# Revit family: ewf_ewg-40_60eta2_fta2-h_60Hz
name_source: partatom
category: 機械設備
units: mm (PartAtom-declared; Revit-internal decimal feet)

## family parameters
OmniClass タイトル = Industrial Ventilating Equipment
OmniClass 番号 = 23.75.35.21.17
パーツ タイプ = 標準
ロード時にボイドで切り取り = はい
丸型コネクタ寸法 = 直径を使用
作業面ベース = いいえ
共有 = いいえ
常に垂直 = はい
部屋計算ポイント = はい

## types (6) — shared parameters
IfcExportAs = IfcFanType
IfcExportType = TUBEAXIAL
MID風量 = 0.0 m³/h
MIN風量 = 0.0 m³/h
OmniClassCode = 23-33 31 19 11 17
URL = https://www.mitsubishielectric.co.jp
Uniclass2015Code = Pr_65_67_29_67
Uniclass2015Title = Propeller fans
Uniclass2015Version = Systems v1.9
ファンの種類 = 軸流羽根
フレームの厚さ = 10  [stored 0.0328084 ft]
仕様書バージョン = Version1.0
企業コード = 108420
分類コード = 50052503100110
周波数 = 60 Hz
呼称 = 有圧扇
極数 = 3
法定耐用年数 = 15
相 = 3
製品リリース年月 = 2022年6月1日
製品出荷対象 = 国内
製造元 = 三菱電機株式会社
設置方法 = 壁付
説明 = 産業用有圧換気扇 低騒音形 耐熱タイプ 排気専用
負荷分類 = 3_ファン類
運転質量 = 0.00 kg

## per-type parameters (varying)
| type | Depth | Height | MAX風量 | Width | オリフィス_Depth | オリフィス径 | モデル | モーター径 | レグ_Depth | レグ_Height | レグ_Width | 価格 | 極 | 消費電力 | 羽根径 | 製品質量 | 質量 | 電動機出力 | 電圧 |
| EWF-40ETA2-H_200V | 308  [stored 1.0105 ft] | 520  [stored 1.70604 ft] | 5520.0 m³/h | 520  [stored 1.70604 ft] | 99  [stored 0.324803 ft] | 480  [stored 1.5748 ft] | EWF-40ETA2-H | 131  [stored 0.42979 ft] | 279 | 416  [stored 1.36483 ft] | 416  [stored 1.36483 ft] | 185000 $ | 4 | 325 W | ∅400 | 16.60 kg | 19.92 kg | 400 W | 200 V |
| EWF-50FTA2-H_200V | 327 | 620  [stored 2.03412 ft] | 8280.0 m³/h | 620  [stored 2.03412 ft] | 84  [stored 0.275591 ft] | 590  [stored 1.9357 ft] | EWF-50FTA2-H | 200  [stored 0.656168 ft] | 242  [stored 0.793963 ft] | 516  [stored 1.69291 ft] | 516  [stored 1.69291 ft] | 231000 $ | 4 | 512 W | ∅500 | 25.00 kg | 30.00 kg | 750 W | 200 V |
| EWG-60FTA2-H_200V | 375  [stored 1.23031 ft] | 710 | 11160.0 m³/h | 710 | 119  [stored 0.39042 ft] | 703  [stored 2.30643 ft] | EWG-60FTA2-H | 200  [stored 0.656168 ft] | 290  [stored 0.951444 ft] | 606  [stored 1.98819 ft] | 606  [stored 1.98819 ft] | 286000 $ | 6 | 580 W | ∅600 | 29.00 kg | 34.80 kg | 750 W | 200 V |
| EWF-40ETA2-H_220V | 308  [stored 1.0105 ft] | 520  [stored 1.70604 ft] | 5520.0 m³/h | 520  [stored 1.70604 ft] | 99  [stored 0.324803 ft] | 480  [stored 1.5748 ft] | EWF-40ETA2-H | 131  [stored 0.42979 ft] | 279 | 416  [stored 1.36483 ft] | 416  [stored 1.36483 ft] | 185000 $ | 4 | 330 W | ∅400 | 16.60 kg | 19.92 kg | 400 W | 220 V |
| EWF-50FTA2-H_220V | 327 | 620  [stored 2.03412 ft] | 8280.0 m³/h | 620  [stored 2.03412 ft] | 84  [stored 0.275591 ft] | 590  [stored 1.9357 ft] | EWF-50FTA2-H | 200  [stored 0.656168 ft] | 242  [stored 0.793963 ft] | 516  [stored 1.69291 ft] | 516  [stored 1.69291 ft] | 231000 $ | 4 | 520 W | ∅500 | 25.00 kg | 30.00 kg | 750 W | 220 V |
| EWG-60FTA2-H_220V | 375  [stored 1.23031 ft] | 710 | 11160.0 m³/h | 710 | 119  [stored 0.39042 ft] | 703  [stored 2.30643 ft] | EWG-60FTA2-H | 200  [stored 0.656168 ft] | 290  [stored 0.951444 ft] | 606  [stored 1.98819 ft] | 606  [stored 1.98819 ft] | 286000 $ | 6 | 585 W | ∅600 | 29.00 kg | 34.80 kg | 750 W | 220 V |

note: [stored X ft] marks values corroborated as IEEE doubles in the binary element streams (Revit-internal decimal feet)
